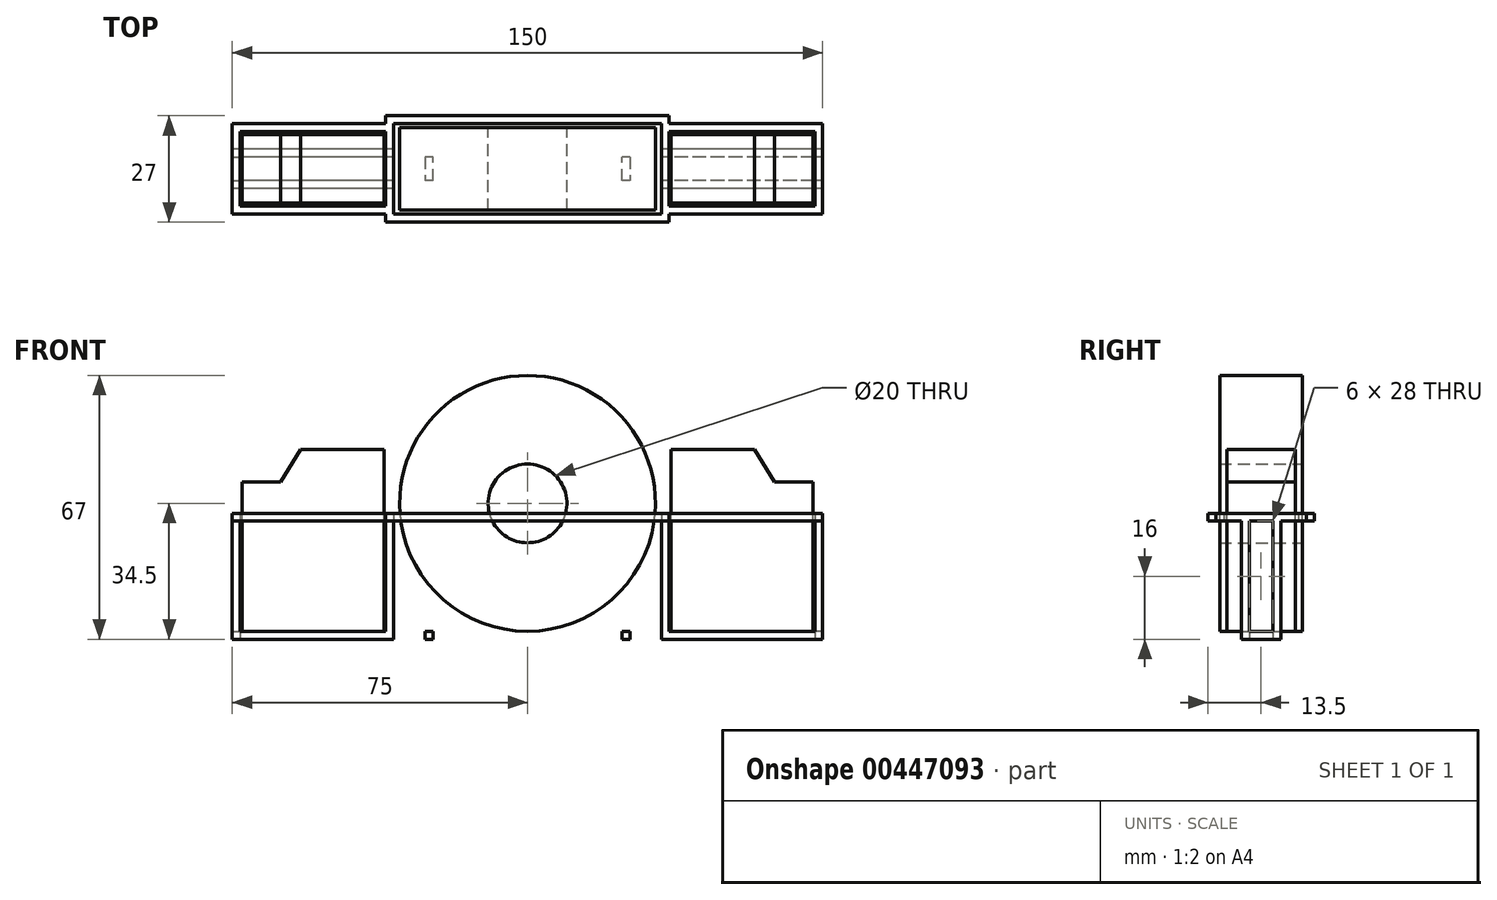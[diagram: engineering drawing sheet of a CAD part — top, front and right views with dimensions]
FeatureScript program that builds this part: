
annotation { "Feature Type Name" : "Feature", "Feature Type Description" : "" }
export const myFeature = defineFeature(function(context is Context, id is Id, definition is map)
    precondition{}
    {
        {
            var Q0;
            Q0=qCreatedBy(makeId("Top.planeOp"),FACE);
            var sketch = newSketch(context, id + "F0", { "sketchPlane" : qUnion([Q0])});
            skLineSegment(sketch, "E0.bottom", {"start": v(75, -5) * mm, "end": v(-75, -5) * mm});
            skLineSegment(sketch, "E0.top", {"start": v(75, 5) * mm, "end": v(-75, 5) * mm});
            skLineSegment(sketch, "E0.left", {"start": v(75, -5) * mm, "end": v(75, 5) * mm});
            skLineSegment(sketch, "E0.right", {"start": v(-75, -5) * mm, "end": v(-75, 5) * mm});
            skPoint(sketch, "E0.middle", {"position": v(0, 0) * mm});
            skLineSegment(sketch, "E1.bottom", {"start": v(73, -3) * mm, "end": v(-73, -3) * mm});
            skLineSegment(sketch, "E1.top", {"start": v(73, 3) * mm, "end": v(-73, 3) * mm});
            skLineSegment(sketch, "E1.left", {"start": v(73, -3) * mm, "end": v(73, 3) * mm});
            skLineSegment(sketch, "E1.right", {"start": v(-73, -3) * mm, "end": v(-73, 3) * mm});
            skLineSegment(sketch, "E2", {"start": v(-26, 3) * mm, "end": v(-26, -3) * mm});
            skLineSegment(sketch, "E3", {"start": v(-26, -3) * mm, "end": v(-24, -3) * mm});
            skLineSegment(sketch, "E4", {"start": v(-24, -3) * mm, "end": v(-24, 3) * mm});
            skLineSegment(sketch, "E5", {"start": v(-24, 3) * mm, "end": v(-26, 3) * mm});
            skLineSegment(sketch, "E6.MirrorCS", {"start": v(24, -3) * mm, "end": v(24, 3) * mm});
            skLineSegment(sketch, "E7.MirrorCS", {"start": v(26, 3) * mm, "end": v(26, -3) * mm});
            skLineSegment(sketch, "E8.bottom", {"start": v(34, -11.5) * mm, "end": v(-34, -11.5) * mm});
            skLineSegment(sketch, "E8.top", {"start": v(34, 11.5) * mm, "end": v(-34, 11.5) * mm});
            skLineSegment(sketch, "E8.left", {"start": v(34, -11.5) * mm, "end": v(34, 11.5) * mm});
            skLineSegment(sketch, "E8.right", {"start": v(-34, -11.5) * mm, "end": v(-34, 11.5) * mm});
            skLineSegment(sketch, "E9.0", {"start": v(36, 13.5) * mm, "end": v(-36, 13.5) * mm});
            skLineSegment(sketch, "E9.1", {"start": v(36, -13.5) * mm, "end": v(36, 13.5) * mm});
            skLineSegment(sketch, "E9.2", {"start": v(36, -13.5) * mm, "end": v(-36, -13.5) * mm});
            skLineSegment(sketch, "E9.3", {"start": v(-36, -13.5) * mm, "end": v(-36, 13.5) * mm});
            skLineSegment(sketch, "E10", {"start": v(-36, 9.5) * mm, "end": v(-73, 9.5) * mm});
            skLineSegment(sketch, "E11", {"start": v(-73, 9.5) * mm, "end": v(-73, 0) * mm});
            skLineSegment(sketch, "E12.MirrorCS", {"start": v(-73, -9.5) * mm, "end": v(-73, 0) * mm});
            skLineSegment(sketch, "E13.MirrorCS", {"start": v(-36, -9.5) * mm, "end": v(-73, -9.5) * mm});
            skLineSegment(sketch, "E14.0", {"start": v(-36, -11.5) * mm, "end": v(-75, -11.5) * mm});
            skLineSegment(sketch, "E14.1", {"start": v(-75, -11.5) * mm, "end": v(-75, 0) * mm});
            skLineSegment(sketch, "E14.2", {"start": v(-75, 11.5) * mm, "end": v(-75, 0) * mm});
            skLineSegment(sketch, "E14.3", {"start": v(-36, 11.5) * mm, "end": v(-75, 11.5) * mm});
            skLineSegment(sketch, "E15.MirrorCS", {"start": v(36, 11.5) * mm, "end": v(75, 11.5) * mm});
            skLineSegment(sketch, "E16.MirrorCS", {"start": v(36, 9.5) * mm, "end": v(73, 9.5) * mm});
            skLineSegment(sketch, "E17.MirrorCS", {"start": v(75, 11.5) * mm, "end": v(75, 0) * mm});
            skLineSegment(sketch, "E18.MirrorCS", {"start": v(73, 9.5) * mm, "end": v(73, 0) * mm});
            skLineSegment(sketch, "E19.MirrorCS", {"start": v(75, -11.5) * mm, "end": v(75, 0) * mm});
            skLineSegment(sketch, "E20.MirrorCS", {"start": v(73, -9.5) * mm, "end": v(73, 0) * mm});
            skLineSegment(sketch, "E21.MirrorCS", {"start": v(36, -9.5) * mm, "end": v(73, -9.5) * mm});
            skLineSegment(sketch, "E22.MirrorCS", {"start": v(36, -11.5) * mm, "end": v(75, -11.5) * mm});
            skPoint(sketch, "E23", {"position": v(-73, 5) * mm});
            skPoint(sketch, "E24", {"position": v(-75, 3) * mm});
            skPoint(sketch, "E25", {"position": v(-73, 3) * mm});
            skPoint(sketch, "E26", {"position": v(-75, 5) * mm});
            skPoint(sketch, "E27", {"position": v(-73, -3) * mm});
            skPoint(sketch, "E28", {"position": v(-75, -3) * mm});
            skPoint(sketch, "E29", {"position": v(-75, -5) * mm});
            skPoint(sketch, "E30", {"position": v(-73, -5) * mm});
            skPoint(sketch, "E31", {"position": v(-36, 5) * mm});
            skPoint(sketch, "E32", {"position": v(-34, 5) * mm});
            skPoint(sketch, "E33", {"position": v(-34, 3) * mm});
            skPoint(sketch, "E34", {"position": v(-36, 3) * mm});
            skPoint(sketch, "E35", {"position": v(-36, -3) * mm});
            skPoint(sketch, "E36", {"position": v(-34, -3) * mm});
            skPoint(sketch, "E37", {"position": v(-34, -5) * mm});
            skPoint(sketch, "E38", {"position": v(-36, -5) * mm});
            skPoint(sketch, "E39", {"position": v(34, 5) * mm});
            skPoint(sketch, "E40", {"position": v(36, 5) * mm});
            skPoint(sketch, "E41", {"position": v(36, 3) * mm});
            skPoint(sketch, "E42", {"position": v(34, 3) * mm});
            skPoint(sketch, "E43", {"position": v(34, -3) * mm});
            skPoint(sketch, "E44", {"position": v(36, -3) * mm});
            skPoint(sketch, "E45", {"position": v(34, -5) * mm});
            skPoint(sketch, "E46", {"position": v(36, -5) * mm});
            skPoint(sketch, "E47", {"position": v(73, 5) * mm});
            skPoint(sketch, "E48", {"position": v(75, 5) * mm});
            skPoint(sketch, "E49", {"position": v(73, 3) * mm});
            skPoint(sketch, "E50", {"position": v(75, 3) * mm});
            skPoint(sketch, "E51", {"position": v(73, -3) * mm});
            skPoint(sketch, "E52", {"position": v(73, -5) * mm});
            skPoint(sketch, "E53", {"position": v(75, -5) * mm});
            skPoint(sketch, "E54", {"position": v(75, -3) * mm});
            skLineSegment(sketch, "E55", {"start": v(73, 3) * mm, "end": v(75, 3) * mm});
            skLineSegment(sketch, "E56", {"start": v(73, -3) * mm, "end": v(75, -3) * mm});
            skLineSegment(sketch, "E57", {"start": v(-73, 3) * mm, "end": v(-75, 3) * mm});
            skLineSegment(sketch, "E58", {"start": v(-73, -3) * mm, "end": v(-75, -3) * mm});
            skSolve(sketch);
        }
        {
            var Q0;
            {var subQ0=sQuery(id+"F0.wireOp",EDGE,"E9.3");var subQ1=sQuery(id+"F0.wireOp",EDGE,"E0.top");var subQ2=makeQuery(id+"F0.imprint","INTERSECT",VERTEX,{"derivedFrom":[subQ1,subQ0]});Q0=makeQuery(id+"F0.imprint","IMPRINT",FACE,{"disambiguationData":[TD([[makeQuery(id+"F0.imprint","IMPRINT",EDGE,{"disambiguationData":[TD([[subQ2,-1.0]])],"derivedFrom":subQ1}),1.0]])]});}
            var Q1;
            {var subQ3=sQuery(id+"F0.wireOp",EDGE,"E57");Q1=makeQuery(id+"F0.imprint","IMPRINT",FACE,{"disambiguationData":[TD([[makeQuery(id+"F0.imprint","IMPRINT",EDGE,{"derivedFrom":subQ3}),1.0]])]});}
            var Q2;
            {var subQ5=sQuery(id+"F0.wireOp",EDGE,"E57");Q2=makeQuery(id+"F0.imprint","IMPRINT",FACE,{"disambiguationData":[TD([[makeQuery(id+"F0.imprint","IMPRINT",EDGE,{"derivedFrom":subQ5}),-1.0]])]});}
            var Q3;
            {var subQ5=sQuery(id+"F0.wireOp",EDGE,"E58");Q3=makeQuery(id+"F0.imprint","IMPRINT",FACE,{"disambiguationData":[TD([[makeQuery(id+"F0.imprint","IMPRINT",EDGE,{"derivedFrom":subQ5}),1.0]])]});}
            var Q4;
            {var subQ0=sQuery(id+"F0.wireOp",EDGE,"E9.3");var subQ1=sQuery(id+"F0.wireOp",EDGE,"E0.bottom");var subQ2=makeQuery(id+"F0.imprint","INTERSECT",VERTEX,{"derivedFrom":[subQ1,subQ0]});Q4=makeQuery(id+"F0.imprint","IMPRINT",FACE,{"disambiguationData":[TD([[makeQuery(id+"F0.imprint","IMPRINT",EDGE,{"disambiguationData":[TD([[subQ2,-1.0]])],"derivedFrom":subQ1}),-1.0]])]});}
            var Q5;
            {var subQ0=sQuery(id+"F0.wireOp",EDGE,"E8.right");var subQ1=sQuery(id+"F0.wireOp",EDGE,"E0.bottom");var subQ2=makeQuery(id+"F0.imprint","INTERSECT",VERTEX,{"derivedFrom":[subQ1,subQ0]});Q5=makeQuery(id+"F0.imprint","IMPRINT",FACE,{"disambiguationData":[TD([[makeQuery(id+"F0.imprint","IMPRINT",EDGE,{"disambiguationData":[TD([[subQ2,-1.0]])],"derivedFrom":subQ1}),-1.0]])]});}
            var Q6;
            {var subQ0=sQuery(id+"F0.wireOp",EDGE,"E8.right");var subQ1=sQuery(id+"F0.wireOp",EDGE,"E0.top");var subQ2=makeQuery(id+"F0.imprint","INTERSECT",VERTEX,{"derivedFrom":[subQ1,subQ0]});Q6=makeQuery(id+"F0.imprint","IMPRINT",FACE,{"disambiguationData":[TD([[makeQuery(id+"F0.imprint","IMPRINT",EDGE,{"disambiguationData":[TD([[subQ2,-1.0]])],"derivedFrom":subQ1}),1.0]])]});}
            var Q7;
            {var subQ0=sQuery(id+"F0.wireOp",EDGE,"E5");Q7=makeQuery(id+"F0.imprint","IMPRINT",FACE,{"disambiguationData":[TD([[makeQuery(id+"F0.imprint","IMPRINT",EDGE,{"derivedFrom":subQ0}),-1.0]])]});}
            var Q8;
            Q8=makeQuery(id+"F0.imprint","IMPRINT",FACE,{"disambiguationData":[TD([[makeQuery(id+"F0.imprint","IMPRINT",EDGE,{"derivedFrom":sQuery(id+"F0.wireOp",EDGE,"E2")}),1.0]])]});
            var Q9;
            {var subQ7=sQuery(id+"F0.wireOp",EDGE,"E3");Q9=makeQuery(id+"F0.imprint","IMPRINT",FACE,{"disambiguationData":[TD([[makeQuery(id+"F0.imprint","IMPRINT",EDGE,{"derivedFrom":subQ7}),-1.0]])]});}
            var Q10;
            {var subQ0=sQuery(id+"F0.wireOp",EDGE,"E6.MirrorCS");Q10=makeQuery(id+"F0.imprint","IMPRINT",FACE,{"disambiguationData":[TD([[makeQuery(id+"F0.imprint","IMPRINT",EDGE,{"derivedFrom":subQ0}),-1.0]])]});}
            var Q11;
            {var subQ0=sQuery(id+"F0.wireOp",EDGE,"E9.1");var subQ1=sQuery(id+"F0.wireOp",EDGE,"E0.top");var subQ2=makeQuery(id+"F0.imprint","INTERSECT",VERTEX,{"derivedFrom":[subQ1,subQ0]});Q11=makeQuery(id+"F0.imprint","IMPRINT",FACE,{"disambiguationData":[TD([[makeQuery(id+"F0.imprint","IMPRINT",EDGE,{"disambiguationData":[TD([[subQ2,-1.0]])],"derivedFrom":subQ1}),1.0]])]});}
            var Q12;
            {var subQ0=sQuery(id+"F0.wireOp",EDGE,"E9.1");var subQ1=sQuery(id+"F0.wireOp",EDGE,"E0.bottom");var subQ2=makeQuery(id+"F0.imprint","INTERSECT",VERTEX,{"derivedFrom":[subQ1,subQ0]});Q12=makeQuery(id+"F0.imprint","IMPRINT",FACE,{"disambiguationData":[TD([[makeQuery(id+"F0.imprint","IMPRINT",EDGE,{"disambiguationData":[TD([[subQ2,-1.0]])],"derivedFrom":subQ1}),-1.0]])]});}
            var Q13;
            {var subQ0=sQuery(id+"F0.wireOp",EDGE,"E18.MirrorCS");var subQ1=sQuery(id+"F0.wireOp",EDGE,"E0.top");var subQ2=makeQuery(id+"F0.imprint","INTERSECT",VERTEX,{"derivedFrom":[subQ1,subQ0]});Q13=makeQuery(id+"F0.imprint","IMPRINT",FACE,{"disambiguationData":[TD([[makeQuery(id+"F0.imprint","IMPRINT",EDGE,{"disambiguationData":[TD([[subQ2,-1.0]])],"derivedFrom":subQ1}),1.0]])]});}
            var Q14;
            {var subQ0=sQuery(id+"F0.wireOp",EDGE,"E20.MirrorCS");var subQ1=sQuery(id+"F0.wireOp",EDGE,"E0.bottom");var subQ2=makeQuery(id+"F0.imprint","INTERSECT",VERTEX,{"derivedFrom":[subQ1,subQ0]});Q14=makeQuery(id+"F0.imprint","IMPRINT",FACE,{"disambiguationData":[TD([[makeQuery(id+"F0.imprint","IMPRINT",EDGE,{"disambiguationData":[TD([[subQ2,-1.0]])],"derivedFrom":subQ1}),-1.0]])]});}
            var Q15;
            {var subQ5=sQuery(id+"F0.wireOp",EDGE,"E55");Q15=makeQuery(id+"F0.imprint","IMPRINT",FACE,{"disambiguationData":[TD([[makeQuery(id+"F0.imprint","IMPRINT",EDGE,{"derivedFrom":subQ5}),1.0]])]});}
            var Q16;
            {var subQ7=sQuery(id+"F0.wireOp",EDGE,"E55");Q16=makeQuery(id+"F0.imprint","IMPRINT",FACE,{"disambiguationData":[TD([[makeQuery(id+"F0.imprint","IMPRINT",EDGE,{"derivedFrom":subQ7}),-1.0]])]});}
            var Q17;
            {var subQ5=sQuery(id+"F0.wireOp",EDGE,"E56");Q17=makeQuery(id+"F0.imprint","IMPRINT",FACE,{"disambiguationData":[TD([[makeQuery(id+"F0.imprint","IMPRINT",EDGE,{"derivedFrom":subQ5}),-1.0]])]});}
            extrude(context, id + "F1", {"entities" : qUnion([Q0, Q1, Q2, Q3, Q4, Q5, Q6, Q7, Q8, Q9, Q10, Q11, Q12, Q13, Q14, Q15, Q16, Q17]), "depth" : 2 * mm, "offsetDistance" : 25 * mm});
        }
        {
            var Q0;
            {var subQ5=sQuery(id+"F0.wireOp",EDGE,"E57");Q0=makeQuery(id+"F0.imprint","IMPRINT",FACE,{"disambiguationData":[TD([[makeQuery(id+"F0.imprint","IMPRINT",EDGE,{"derivedFrom":subQ5}),-1.0]])]});}
            var Q1;
            {var subQ5=sQuery(id+"F0.wireOp",EDGE,"E58");Q1=makeQuery(id+"F0.imprint","IMPRINT",FACE,{"disambiguationData":[TD([[makeQuery(id+"F0.imprint","IMPRINT",EDGE,{"derivedFrom":subQ5}),1.0]])]});}
            var Q2;
            {var subQ0=sQuery(id+"F0.wireOp",EDGE,"E8.right");var subQ1=sQuery(id+"F0.wireOp",EDGE,"E0.top");var subQ2=makeQuery(id+"F0.imprint","INTERSECT",VERTEX,{"derivedFrom":[subQ1,subQ0]});Q2=makeQuery(id+"F0.imprint","IMPRINT",FACE,{"disambiguationData":[TD([[makeQuery(id+"F0.imprint","IMPRINT",EDGE,{"disambiguationData":[TD([[subQ2,-1.0]])],"derivedFrom":subQ1}),1.0]])]});}
            var Q3;
            {var subQ0=sQuery(id+"F0.wireOp",EDGE,"E8.right");var subQ1=sQuery(id+"F0.wireOp",EDGE,"E0.bottom");var subQ2=makeQuery(id+"F0.imprint","INTERSECT",VERTEX,{"derivedFrom":[subQ1,subQ0]});Q3=makeQuery(id+"F0.imprint","IMPRINT",FACE,{"disambiguationData":[TD([[makeQuery(id+"F0.imprint","IMPRINT",EDGE,{"disambiguationData":[TD([[subQ2,-1.0]])],"derivedFrom":subQ1}),-1.0]])]});}
            var Q4;
            {var subQ0=sQuery(id+"F0.wireOp",EDGE,"E9.1");var subQ1=sQuery(id+"F0.wireOp",EDGE,"E0.top");var subQ2=makeQuery(id+"F0.imprint","INTERSECT",VERTEX,{"derivedFrom":[subQ1,subQ0]});Q4=makeQuery(id+"F0.imprint","IMPRINT",FACE,{"disambiguationData":[TD([[makeQuery(id+"F0.imprint","IMPRINT",EDGE,{"disambiguationData":[TD([[subQ2,-1.0]])],"derivedFrom":subQ1}),1.0]])]});}
            var Q5;
            {var subQ0=sQuery(id+"F0.wireOp",EDGE,"E9.1");var subQ1=sQuery(id+"F0.wireOp",EDGE,"E0.bottom");var subQ2=makeQuery(id+"F0.imprint","INTERSECT",VERTEX,{"derivedFrom":[subQ1,subQ0]});Q5=makeQuery(id+"F0.imprint","IMPRINT",FACE,{"disambiguationData":[TD([[makeQuery(id+"F0.imprint","IMPRINT",EDGE,{"disambiguationData":[TD([[subQ2,-1.0]])],"derivedFrom":subQ1}),-1.0]])]});}
            var Q6;
            {var subQ5=sQuery(id+"F0.wireOp",EDGE,"E55");Q6=makeQuery(id+"F0.imprint","IMPRINT",FACE,{"disambiguationData":[TD([[makeQuery(id+"F0.imprint","IMPRINT",EDGE,{"derivedFrom":subQ5}),1.0]])]});}
            var Q7;
            {var subQ5=sQuery(id+"F0.wireOp",EDGE,"E56");Q7=makeQuery(id+"F0.imprint","IMPRINT",FACE,{"disambiguationData":[TD([[makeQuery(id+"F0.imprint","IMPRINT",EDGE,{"derivedFrom":subQ5}),-1.0]])]});}
            extrude(context, id + "F2", {"entities" : qUnion([Q0, Q1, Q2, Q3, Q4, Q5, Q6, Q7]), "operationType" : NewBodyOperationType.ADD, "depth" : 30 * mm, "offsetDistance" : 25 * mm});
        }
        {
            var Q0;
            {var subQ1=sQuery(id+"F0.wireOp",EDGE,"E15.MirrorCS");Q0=makeQuery(id+"F0.imprint","IMPRINT",FACE,{"disambiguationData":[TD([[makeQuery(id+"F0.imprint","IMPRINT",EDGE,{"derivedFrom":subQ1}),-1.0]])]});}
            var Q1;
            {var subQ5=sQuery(id+"F0.wireOp",EDGE,"E55");Q1=makeQuery(id+"F0.imprint","IMPRINT",FACE,{"disambiguationData":[TD([[makeQuery(id+"F0.imprint","IMPRINT",EDGE,{"derivedFrom":subQ5}),1.0]])]});}
            var Q2;
            {var subQ7=sQuery(id+"F0.wireOp",EDGE,"E55");Q2=makeQuery(id+"F0.imprint","IMPRINT",FACE,{"disambiguationData":[TD([[makeQuery(id+"F0.imprint","IMPRINT",EDGE,{"derivedFrom":subQ7}),-1.0]])]});}
            var Q3;
            {var subQ5=sQuery(id+"F0.wireOp",EDGE,"E56");Q3=makeQuery(id+"F0.imprint","IMPRINT",FACE,{"disambiguationData":[TD([[makeQuery(id+"F0.imprint","IMPRINT",EDGE,{"derivedFrom":subQ5}),-1.0]])]});}
            var Q4;
            {var subQ4=sQuery(id+"F0.wireOp",EDGE,"E21.MirrorCS");Q4=makeQuery(id+"F0.imprint","IMPRINT",FACE,{"disambiguationData":[TD([[makeQuery(id+"F0.imprint","IMPRINT",EDGE,{"derivedFrom":subQ4}),-1.0]])]});}
            var Q5;
            {var subQ5=sQuery(id+"F0.wireOp",EDGE,"E8.top");Q5=makeQuery(id+"F0.imprint","IMPRINT",FACE,{"disambiguationData":[TD([[makeQuery(id+"F0.imprint","IMPRINT",EDGE,{"derivedFrom":subQ5}),-1.0]])]});}
            var Q6;
            {var subQ0=sQuery(id+"F0.wireOp",EDGE,"E9.1");var subQ1=sQuery(id+"F0.wireOp",EDGE,"E0.top");var subQ2=makeQuery(id+"F0.imprint","INTERSECT",VERTEX,{"derivedFrom":[subQ1,subQ0]});Q6=makeQuery(id+"F0.imprint","IMPRINT",FACE,{"disambiguationData":[TD([[makeQuery(id+"F0.imprint","IMPRINT",EDGE,{"disambiguationData":[TD([[subQ2,-1.0]])],"derivedFrom":subQ1}),1.0]])]});}
            var Q7;
            {var subQ0=sQuery(id+"F0.wireOp",EDGE,"E9.1");var subQ1=sQuery(id+"F0.wireOp",EDGE,"E1.bottom");var subQ2=makeQuery(id+"F0.imprint","INTERSECT",VERTEX,{"derivedFrom":[subQ1,subQ0]});Q7=makeQuery(id+"F0.imprint","IMPRINT",FACE,{"disambiguationData":[TD([[makeQuery(id+"F0.imprint","IMPRINT",EDGE,{"disambiguationData":[TD([[subQ2,-1.0]])],"derivedFrom":subQ1}),-1.0]])]});}
            var Q8;
            {var subQ0=sQuery(id+"F0.wireOp",EDGE,"E9.1");var subQ1=sQuery(id+"F0.wireOp",EDGE,"E0.bottom");var subQ2=makeQuery(id+"F0.imprint","INTERSECT",VERTEX,{"derivedFrom":[subQ1,subQ0]});Q8=makeQuery(id+"F0.imprint","IMPRINT",FACE,{"disambiguationData":[TD([[makeQuery(id+"F0.imprint","IMPRINT",EDGE,{"disambiguationData":[TD([[subQ2,-1.0]])],"derivedFrom":subQ1}),-1.0]])]});}
            var Q9;
            {var subQ9=sQuery(id+"F0.wireOp",EDGE,"E8.bottom");Q9=makeQuery(id+"F0.imprint","IMPRINT",FACE,{"disambiguationData":[TD([[makeQuery(id+"F0.imprint","IMPRINT",EDGE,{"derivedFrom":subQ9}),1.0]])]});}
            var Q10;
            {var subQ0=sQuery(id+"F0.wireOp",EDGE,"E8.right");var subQ1=sQuery(id+"F0.wireOp",EDGE,"E0.top");var subQ2=makeQuery(id+"F0.imprint","INTERSECT",VERTEX,{"derivedFrom":[subQ1,subQ0]});Q10=makeQuery(id+"F0.imprint","IMPRINT",FACE,{"disambiguationData":[TD([[makeQuery(id+"F0.imprint","IMPRINT",EDGE,{"disambiguationData":[TD([[subQ2,-1.0]])],"derivedFrom":subQ1}),1.0]])]});}
            var Q11;
            {var subQ0=sQuery(id+"F0.wireOp",EDGE,"E8.right");var subQ1=sQuery(id+"F0.wireOp",EDGE,"E1.bottom");var subQ2=makeQuery(id+"F0.imprint","INTERSECT",VERTEX,{"derivedFrom":[subQ1,subQ0]});Q11=makeQuery(id+"F0.imprint","IMPRINT",FACE,{"disambiguationData":[TD([[makeQuery(id+"F0.imprint","IMPRINT",EDGE,{"disambiguationData":[TD([[subQ2,-1.0]])],"derivedFrom":subQ1}),-1.0]])]});}
            var Q12;
            {var subQ0=sQuery(id+"F0.wireOp",EDGE,"E8.right");var subQ1=sQuery(id+"F0.wireOp",EDGE,"E0.bottom");var subQ2=makeQuery(id+"F0.imprint","INTERSECT",VERTEX,{"derivedFrom":[subQ1,subQ0]});Q12=makeQuery(id+"F0.imprint","IMPRINT",FACE,{"disambiguationData":[TD([[makeQuery(id+"F0.imprint","IMPRINT",EDGE,{"disambiguationData":[TD([[subQ2,-1.0]])],"derivedFrom":subQ1}),-1.0]])]});}
            var Q13;
            {var subQ1=sQuery(id+"F0.wireOp",EDGE,"E10");Q13=makeQuery(id+"F0.imprint","IMPRINT",FACE,{"disambiguationData":[TD([[makeQuery(id+"F0.imprint","IMPRINT",EDGE,{"derivedFrom":subQ1}),-1.0]])]});}
            var Q14;
            {var subQ0=sQuery(id+"F0.wireOp",EDGE,"E13.MirrorCS");Q14=makeQuery(id+"F0.imprint","IMPRINT",FACE,{"disambiguationData":[TD([[makeQuery(id+"F0.imprint","IMPRINT",EDGE,{"derivedFrom":subQ0}),1.0]])]});}
            var Q15;
            {var subQ5=sQuery(id+"F0.wireOp",EDGE,"E58");Q15=makeQuery(id+"F0.imprint","IMPRINT",FACE,{"disambiguationData":[TD([[makeQuery(id+"F0.imprint","IMPRINT",EDGE,{"derivedFrom":subQ5}),1.0]])]});}
            var Q16;
            {var subQ3=sQuery(id+"F0.wireOp",EDGE,"E57");Q16=makeQuery(id+"F0.imprint","IMPRINT",FACE,{"disambiguationData":[TD([[makeQuery(id+"F0.imprint","IMPRINT",EDGE,{"derivedFrom":subQ3}),1.0]])]});}
            var Q17;
            {var subQ5=sQuery(id+"F0.wireOp",EDGE,"E57");Q17=makeQuery(id+"F0.imprint","IMPRINT",FACE,{"disambiguationData":[TD([[makeQuery(id+"F0.imprint","IMPRINT",EDGE,{"derivedFrom":subQ5}),-1.0]])]});}
            extrude(context, id + "F3", {"entities" : qUnion([Q0, Q1, Q2, Q3, Q4, Q5, Q6, Q7, Q8, Q9, Q10, Q11, Q12, Q13, Q14, Q15, Q16, Q17]), "operationType" : NewBodyOperationType.ADD, "depth" : 32 * mm, "offsetDistance" : 25 * mm, "hasSecondDirection" : true, "secondDirectionOppositeDirection" : false, "secondDirectionDepth" : 30 * mm});
        }
        {
            var Q0;
            Q0=qCreatedBy(makeId("Front.planeOp"),FACE);
            var sketch = newSketch(context, id + "F4", { "sketchPlane" : qUnion([Q0])});
            skCircle(sketch, "E59", {"center": v(0, 34.5) * mm, "radius": 32.5 * mm});
            skLineSegment(sketch, "E60.bottom", {"start": v(-36.5, 2) * mm, "end": v(-72.5, 2) * mm});
            skLineSegment(sketch, "E60.top", {"start": v(-36.5, 48.25) * mm, "end": v(-57.67, 48.25) * mm});
            skLineSegment(sketch, "E60.left", {"start": v(-36.5, 2) * mm, "end": v(-36.5, 48.25) * mm});
            skLineSegment(sketch, "E60.right", {"start": v(-72.5, 2) * mm, "end": v(-72.5, 40) * mm});
            skLineSegment(sketch, "E61", {"start": v(-72.5, 40) * mm, "end": v(-62.7, 40) * mm});
            skLineSegment(sketch, "E62", {"start": v(-62.7, 40) * mm, "end": v(-57.67, 48.25) * mm});
            skLineSegment(sketch, "E63.MirrorCS", {"start": v(36.5, 2) * mm, "end": v(36.5, 48.25) * mm});
            skLineSegment(sketch, "E64.MirrorCS", {"start": v(36.5, 48.25) * mm, "end": v(57.67, 48.25) * mm});
            skLineSegment(sketch, "E65.MirrorCS", {"start": v(62.7, 40) * mm, "end": v(57.67, 48.25) * mm});
            skLineSegment(sketch, "E66.MirrorCS", {"start": v(72.5, 40) * mm, "end": v(62.7, 40) * mm});
            skLineSegment(sketch, "E67.MirrorCS", {"start": v(72.5, 2) * mm, "end": v(72.5, 40) * mm});
            skLineSegment(sketch, "E68.MirrorCS", {"start": v(36.5, 2) * mm, "end": v(72.5, 2) * mm});
            skCircle(sketch, "E69", {"center": v(0, 34.5) * mm, "radius": 10 * mm});
            skSolve(sketch);
        }
        {
            var Q0;
            Q0=makeQuery(id+"F4.imprint","IMPRINT",FACE,{"disambiguationData":[TD([[makeQuery(id+"F4.imprint","IMPRINT",EDGE,{"derivedFrom":sQuery(id+"F4.wireOp",EDGE,"E60.bottom")}),-1.0]])]});
            var Q1;
            Q1=makeQuery(id+"F4.imprint","IMPRINT",FACE,{"disambiguationData":[TD([[makeQuery(id+"F4.imprint","IMPRINT",EDGE,{"derivedFrom":sQuery(id+"F4.wireOp",EDGE,"E63.MirrorCS")}),-1.0]])]});
            extrude(context, id + "F5", {"entities" : qUnion([Q0, Q1]), "endBound" : BoundingType.SYMMETRIC, "depth" : 17.5 * mm, "offsetDistance" : 25 * mm});
        }
        {
            var Q0;
            Q0=makeQuery(id+"F4.imprint","IMPRINT",FACE,{"disambiguationData":[TD([[makeQuery(id+"F4.imprint","IMPRINT",EDGE,{"derivedFrom":sQuery(id+"F4.wireOp",EDGE,"E59")}),1.0]])]});
            extrude(context, id + "F6", {"entities" : qUnion([Q0]), "endBound" : BoundingType.SYMMETRIC, "depth" : 21 * mm, "offsetDistance" : 25 * mm});
        }
    });
